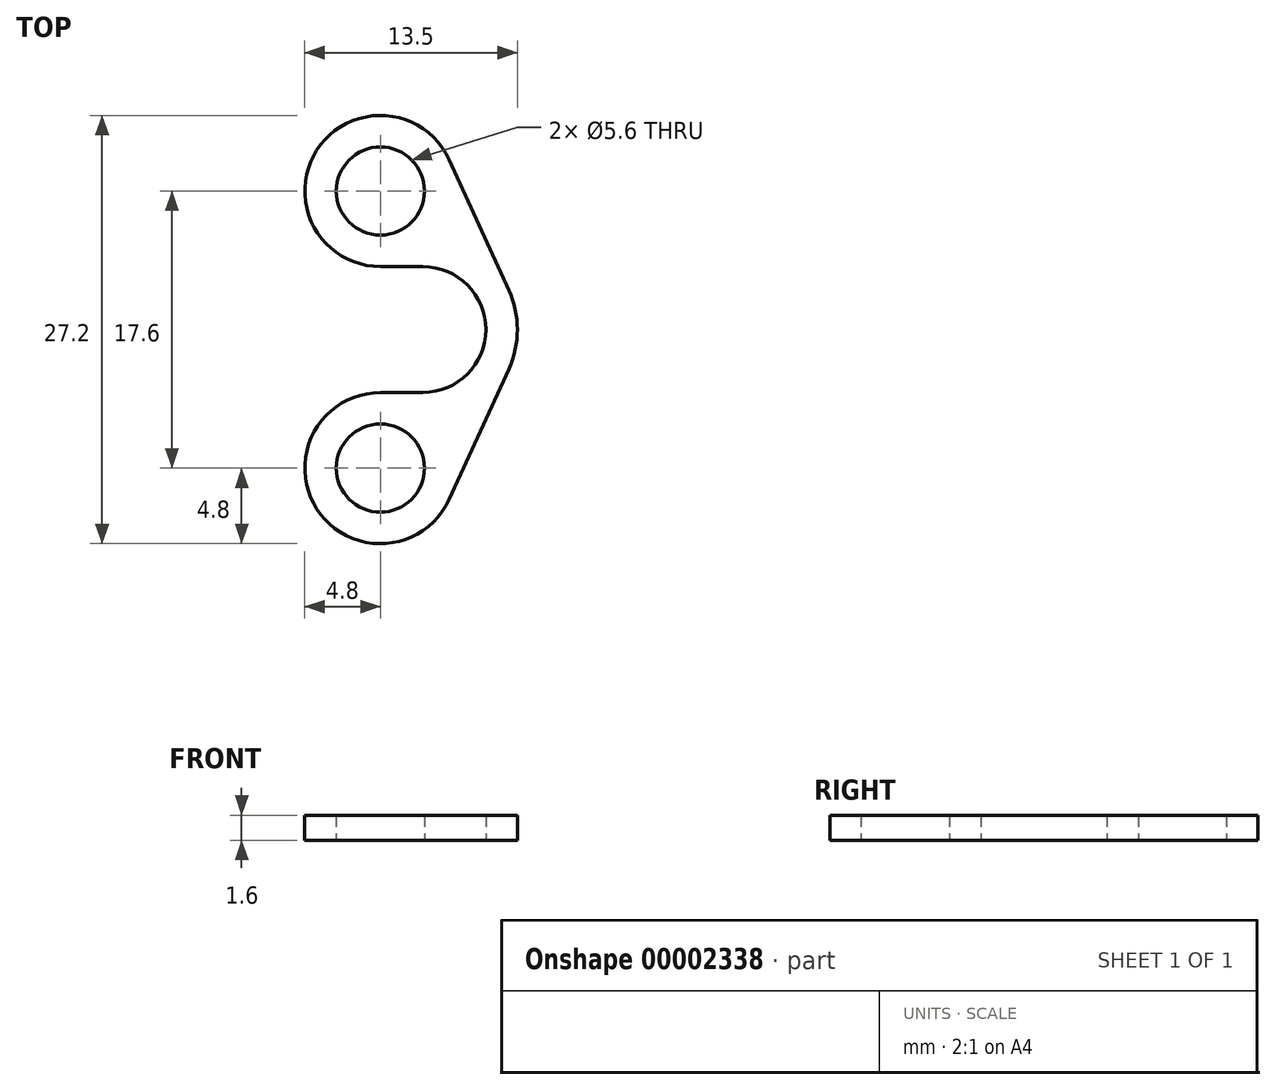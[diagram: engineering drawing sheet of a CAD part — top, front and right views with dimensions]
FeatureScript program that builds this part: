
annotation { "Feature Type Name" : "Feature", "Feature Type Description" : "" }
export const myFeature = defineFeature(function(context is Context, id is Id, definition is map)
    precondition{}
    {
        {
            var Q0;
            Q0=qCreatedBy(makeId("Top.planeOp"),FACE);
            var sketch = newSketch(context, id + "F0", { "sketchPlane" : qUnion([Q0])});
            skCircle(sketch, "E0", {"center": v(-2.7, 8.8) * mm, "radius": 2.8 * mm});
            skCircle(sketch, "E1", {"center": v(-2.7, -8.8) * mm, "radius": 2.8 * mm});
            skArc(sketch, "E2", {"start": v(0, -4) * mm, "mid": v(4, 0) * mm, "end": v(0, 4) * mm});
            skArc(sketch, "E3", {"start": v(1.67, 10.8) * mm, "mid": v(-6.74, 11.4) * mm, "end": v(-2.7, 4) * mm});
            skArc(sketch, "E4", {"start": v(-2.7, -4) * mm, "mid": v(-6.74, -11.4) * mm, "end": v(1.67, -10.8) * mm});
            skLineSegment(sketch, "E5", {"start": v(-2.7, 4) * mm, "end": v(0, 4) * mm});
            skLineSegment(sketch, "E6", {"start": v(-2.7, -4) * mm, "end": v(0, -4) * mm});
            skArc(sketch, "E7", {"start": v(5.46, -2.5) * mm, "mid": v(6, 0) * mm, "end": v(5.46, 2.5) * mm});
            skLineSegment(sketch, "E8", {"start": v(1.67, -10.8) * mm, "end": v(5.46, -2.5) * mm});
            skLineSegment(sketch, "E9", {"start": v(5.46, 2.5) * mm, "end": v(1.67, 10.8) * mm});
            skLineSegment(sketch, "E10", {"start": v(-7.5, 8.8) * mm, "end": v(-7.5, -8.8) * mm, "construction": true});
            skSolve(sketch);
        }
        {
            var Q0;
            Q0 = qSketchRegion(id + "F0", true);
            extrude(context, id + "F1", {"entities" : qUnion([Q0]), "depth" : 1.6 * mm});
        }
    });
